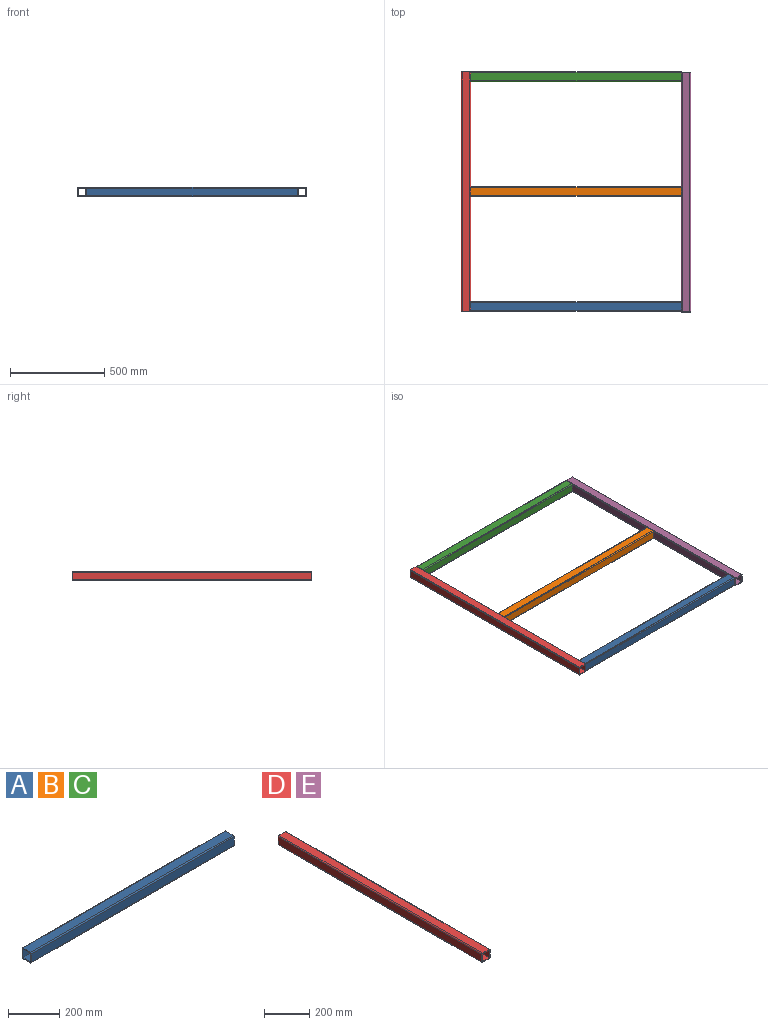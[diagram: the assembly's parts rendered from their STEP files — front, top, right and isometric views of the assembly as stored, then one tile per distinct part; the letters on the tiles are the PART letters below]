
ASSEMBLY  parts=5 mates=4
PART A: 14 faces, bbox 1117.6x50.8x50.8 mm
  f0: plane 50.8x50.8mm, normal (1,0,0), area 854.9mm2, adj f2,f3,f4,f5,f6,f7,f8,f9
  f1: plane 50.8x50.8mm, normal (-1,0,0), area 854.9mm2, adj f2,f3,f4,f5,f6,f7,f8,f9
  f2: plane 1117.6x40.64mm, normal (0,0,-1), area 45419.3mm2, adj f0,f1,f10,f13
  f3: plane 1117.6x40.64mm, normal (0,1,0), area 45419.3mm2, adj f0,f1,f10,f11
  f4: plane 1117.6x40.64mm, normal (0,0,1), area 45419.3mm2, adj f0,f1,f11,f12
  f5: plane 1117.6x40.64mm, normal (0,-1,0), area 45419.3mm2, adj f0,f1,f12,f13
  f6: plane 1117.6x41.28mm, normal (0,0,1), area 46128.9mm2, adj f0,f1,f7,f9
  f7: plane 1117.6x41.28mm, normal (0,-1,0), area 46128.9mm2, adj f0,f1,f6,f8
  f8: plane 1117.6x41.28mm, normal (0,0,-1), area 46128.9mm2, adj f0,f1,f7,f9
  f9: plane 1117.6x41.28mm, normal (0,1,0), area 46128.9mm2, adj f0,f1,f6,f8
  f10: cylinder r=5.08mm len=1117.6mm, axis (1,0,0), area 8918.1mm2, adj f0,f1,f2,f3
  f11: cylinder r=5.08mm len=1117.6mm, axis (-1,0,0), area 8918.1mm2, adj f0,f1,f3,f4
  f12: cylinder r=5.08mm len=1117.6mm, axis (1,0,0), area 8918.1mm2, adj f0,f1,f4,f5
  f13: cylinder r=5.08mm len=1117.6mm, axis (-1,0,0), area 8918.1mm2, adj f0,f1,f2,f5
PART B: same geometry as A
PART C: same geometry as A
PART D: 14 faces, bbox 50.8x1270x50.8 mm
  f0: plane 50.8x50.8mm, normal (0,-1,0), area 854.9mm2, adj f2,f3,f4,f5,f6,f7,f8,f9
  f1: plane 50.8x50.8mm, normal (0,1,0), area 854.9mm2, adj f2,f3,f4,f5,f6,f7,f8,f9
  f2: plane 1270x40.64mm, normal (0,0,-1), area 51612.8mm2, adj f0,f1,f10,f13
  f3: plane 1270x40.64mm, normal (1,0,0), area 51612.8mm2, adj f0,f1,f10,f11
  f4: plane 1270x40.64mm, normal (0,0,1), area 51612.8mm2, adj f0,f1,f11,f12
  f5: plane 1270x40.64mm, normal (-1,0,0), area 51612.8mm2, adj f0,f1,f12,f13
  f6: plane 1270x41.28mm, normal (0,0,1), area 52419.2mm2, adj f0,f1,f7,f9
  f7: plane 1270x41.28mm, normal (-1,0,0), area 52419.2mm2, adj f0,f1,f6,f8
  f8: plane 1270x41.28mm, normal (0,0,-1), area 52419.2mm2, adj f0,f1,f7,f9
  f9: plane 1270x41.28mm, normal (1,0,0), area 52419.2mm2, adj f0,f1,f6,f8
  f10: cylinder r=5.08mm len=1270mm, axis (0,-1,0), area 10134.1mm2, adj f0,f1,f2,f3
  f11: cylinder r=5.08mm len=1270mm, axis (0,1,0), area 10134.1mm2, adj f0,f1,f3,f4
  f12: cylinder r=5.08mm len=1270mm, axis (0,-1,0), area 10134.1mm2, adj f0,f1,f4,f5
  f13: cylinder r=5.08mm len=1270mm, axis (0,1,0), area 10134.1mm2, adj f0,f1,f2,f5
PART E: same geometry as D
PLACE A t=(-10.58,-1231.88,-69.04)mm
PLACE B t=(-10.58,-622.28,-68.73)mm
PLACE C t=(-10.58,-12.68,-69.04)mm
PLACE D t=(-35.98,-622.28,-69.04)mm
PLACE E t=(1132.42,-627.04,-68.73)mm
MATE planar B.f1 <-> D.f3  axis (-1,0,0) through (-10.58,-622.28,-89.36)mm
MATE planar A.f1 <-> D.f3  axis (-1,0,0) through (-10.58,-1257.28,-89.36)mm
MATE planar D.f3 <-> C.f1  axis (1,0,0) through (-10.58,12.72,-89.36)mm
MATE planar C.f0 <-> E.f5  axis (1,0,0) through (1107.02,7.96,-48.41)mm
